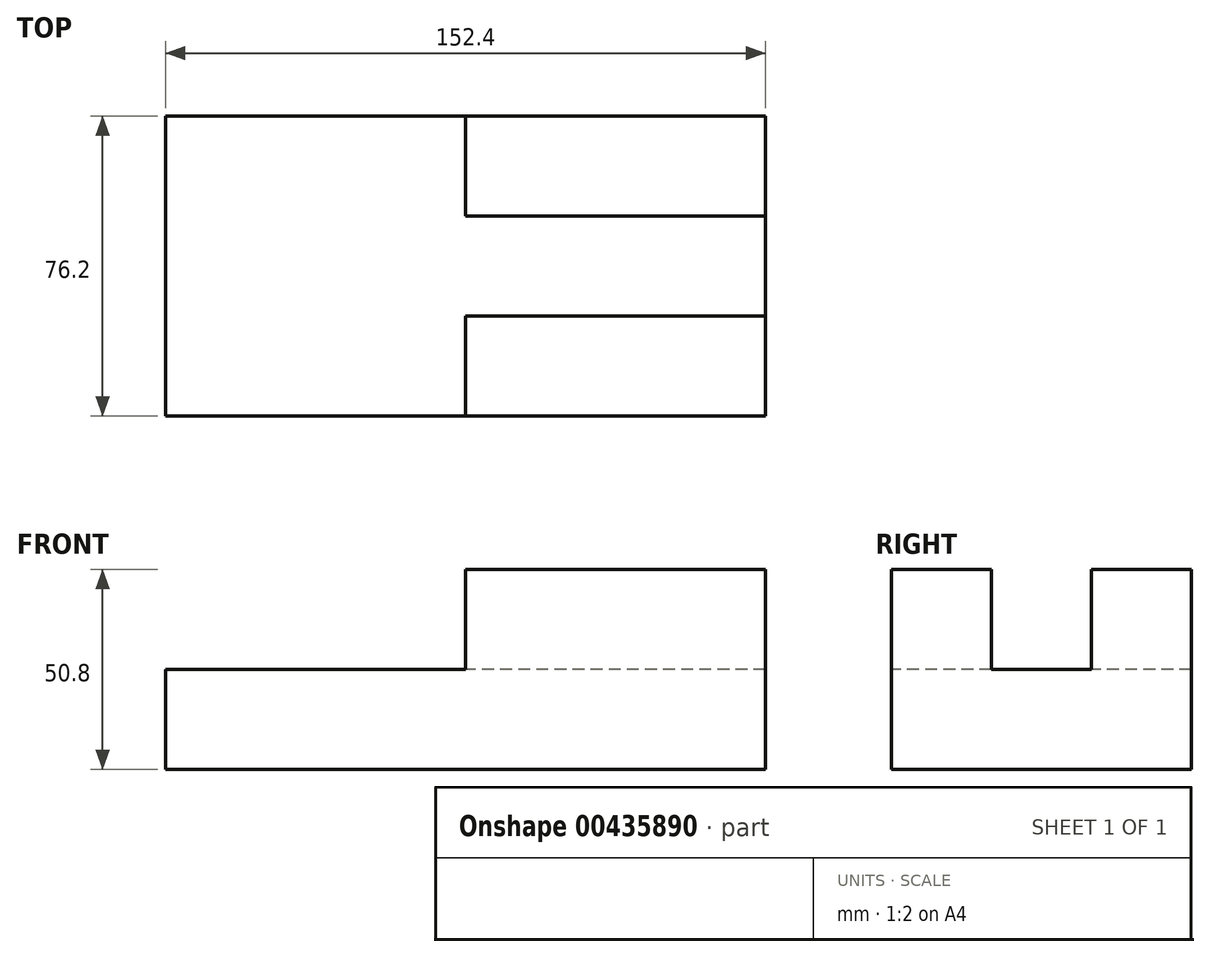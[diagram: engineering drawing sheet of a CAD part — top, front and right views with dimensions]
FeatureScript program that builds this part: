
annotation { "Feature Type Name" : "Feature", "Feature Type Description" : "" }
export const myFeature = defineFeature(function(context is Context, id is Id, definition is map)
    precondition{}
    {
        {
            var Q0;
            Q0=qCreatedBy(makeId("Front.planeOp"),FACE);
            var sketch = newSketch(context, id + "F0", { "sketchPlane" : qUnion([Q0])});
            skLineSegment(sketch, "E0", {"start": v(0, 0) * mm, "end": v(152.4, 0) * mm});
            skLineSegment(sketch, "E1", {"start": v(152.4, 0) * mm, "end": v(152.4, 50.8) * mm});
            skLineSegment(sketch, "E2", {"start": v(0, 0) * mm, "end": v(0, 50.8) * mm});
            skLineSegment(sketch, "E3", {"start": v(0, 50.8) * mm, "end": v(152.4, 50.8) * mm});
            skSolve(sketch);
        }
        {
            var Q0;
            Q0=makeQuery(id+"F0.imprint","IMPRINT",FACE,{"disambiguationData":[TD([[makeQuery(id+"F0.imprint","IMPRINT",EDGE,{"derivedFrom":sQuery(id+"F0.wireOp",EDGE,"E0")}),1.0]])]});
            extrude(context, id + "F1", {"entities" : qUnion([Q0]), "oppositeDirection" : true, "depth" : 76.2 * mm});
        }
        {
            var Q0;
            Q0=makeQuery(id+"F1.opExtrude","CAP_FACE",FACE,{"disambiguationData":[OSD([sQuery(id+"F0.wireOp",EDGE,"E0"),sQuery(id+"F0.wireOp",EDGE,"E1"),sQuery(id+"F0.wireOp",EDGE,"E2"),sQuery(id+"F0.wireOp",EDGE,"E3")])],"isStart":true});
            var sketch = newSketch(context, id + "F2", { "sketchPlane" : qUnion([Q0])});
            skLineSegment(sketch, "E4", {"start": v(0, 25.4) * mm, "end": v(76.2, 25.4) * mm});
            skLineSegment(sketch, "E5", {"start": v(76.2, 25.4) * mm, "end": v(76.2, 50.8) * mm});
            skLineSegment(sketch, "E6", {"start": v(0, 25.4) * mm, "end": v(0, 50.8) * mm});
            skLineSegment(sketch, "E7", {"start": v(0, 50.8) * mm, "end": v(76.2, 50.8) * mm});
            skSolve(sketch);
        }
        {
            var Q0;
            Q0=makeQuery(id+"F2.imprint","IMPRINT",FACE,{"disambiguationData":[TD([[makeQuery(id+"F2.imprint","IMPRINT",EDGE,{"derivedFrom":sQuery(id+"F2.wireOp",EDGE,"E4")}),1.0]])]});
            extrude(context, id + "F3", {"entities" : qUnion([Q0]), "operationType" : NewBodyOperationType.REMOVE, "oppositeDirection" : true, "depth" : 76.2 * mm});
        }
        {
            var Q0;
            Q0=qCreatedBy(makeId("Right.planeOp"),FACE);
            var sketch = newSketch(context, id + "F4", { "sketchPlane" : qUnion([Q0])});
            skLineSegment(sketch, "E8", {"start": v(0, 0) * mm, "end": v(0, 50.8) * mm});
            skLineSegment(sketch, "E9", {"start": v(0, 50.8) * mm, "end": v(25.4, 50.8) * mm});
            skLineSegment(sketch, "E10", {"start": v(25.4, 50.8) * mm, "end": v(25.4, 25.4) * mm});
            skLineSegment(sketch, "E11", {"start": v(25.4, 25.4) * mm, "end": v(50.8, 25.4) * mm});
            skLineSegment(sketch, "E12", {"start": v(50.8, 25.4) * mm, "end": v(50.8, 50.8) * mm});
            skLineSegment(sketch, "E13", {"start": v(50.8, 50.8) * mm, "end": v(76.2, 50.8) * mm});
            skLineSegment(sketch, "E14", {"start": v(25.4, 50.8) * mm, "end": v(50.8, 50.8) * mm});
            skLineSegment(sketch, "E15", {"start": v(34.78, 41.44) * mm, "end": v(25.4, 41.44) * mm});
            skLineSegment(sketch, "E16", {"start": v(25.4, 41.44) * mm, "end": v(-20.5, 113.13) * mm});
            skLineSegment(sketch, "E17", {"start": v(-20.5, 113.13) * mm, "end": v(-47.78, 134.43) * mm});
            skSolve(sketch);
        }
        {
            var Q0;
            {var subQ0=sQuery(id+"F4.wireOp",EDGE,"E11");Q0=makeQuery(id+"F4.imprint","IMPRINT",FACE,{"disambiguationData":[TD([[makeQuery(id+"F4.imprint","IMPRINT",EDGE,{"derivedFrom":subQ0}),1.0]])]});}
            extrude(context, id + "F5", {"entities" : qUnion([Q0]), "operationType" : NewBodyOperationType.REMOVE, "depth" : 152.4 * mm});
        }
    });
